AUTODESK INVENTOR PART (.ipt)
format: ipt  version: 2014 SP1 (Build 180222100, 222)  size: 93,184 bytes
history: native  units: in
note: dims shown in document units (in); Inventor stores cm internally (conversion verified against a paired STEP export)
features: sketch x1
ambient origin geometry x8: Origin, YZ Plane, XZ Plane, XY Plane, X Axis, Y Axis, Z Axis, Center Point
feature tree (1):
  sketch  "Sketch1"  dims[d0=1.0in d1=27.0in d2=2.0625in d3=1.3125in d4=3.3125in d5=5.125in d6=25.0in d7=6.0in d8=5.0in d9=5.0in d10=12.0in d11=4.0in d13=20.0in d14=15.0in d15=6.0in d16=6.0in d17=7.0in d18=9.0in d20=11.0in d21=6.0in d22=15.0in d23=6.0in d24=9.0in d25=2.7in d26=10.761in d28=25.0in d29=17.0in]
